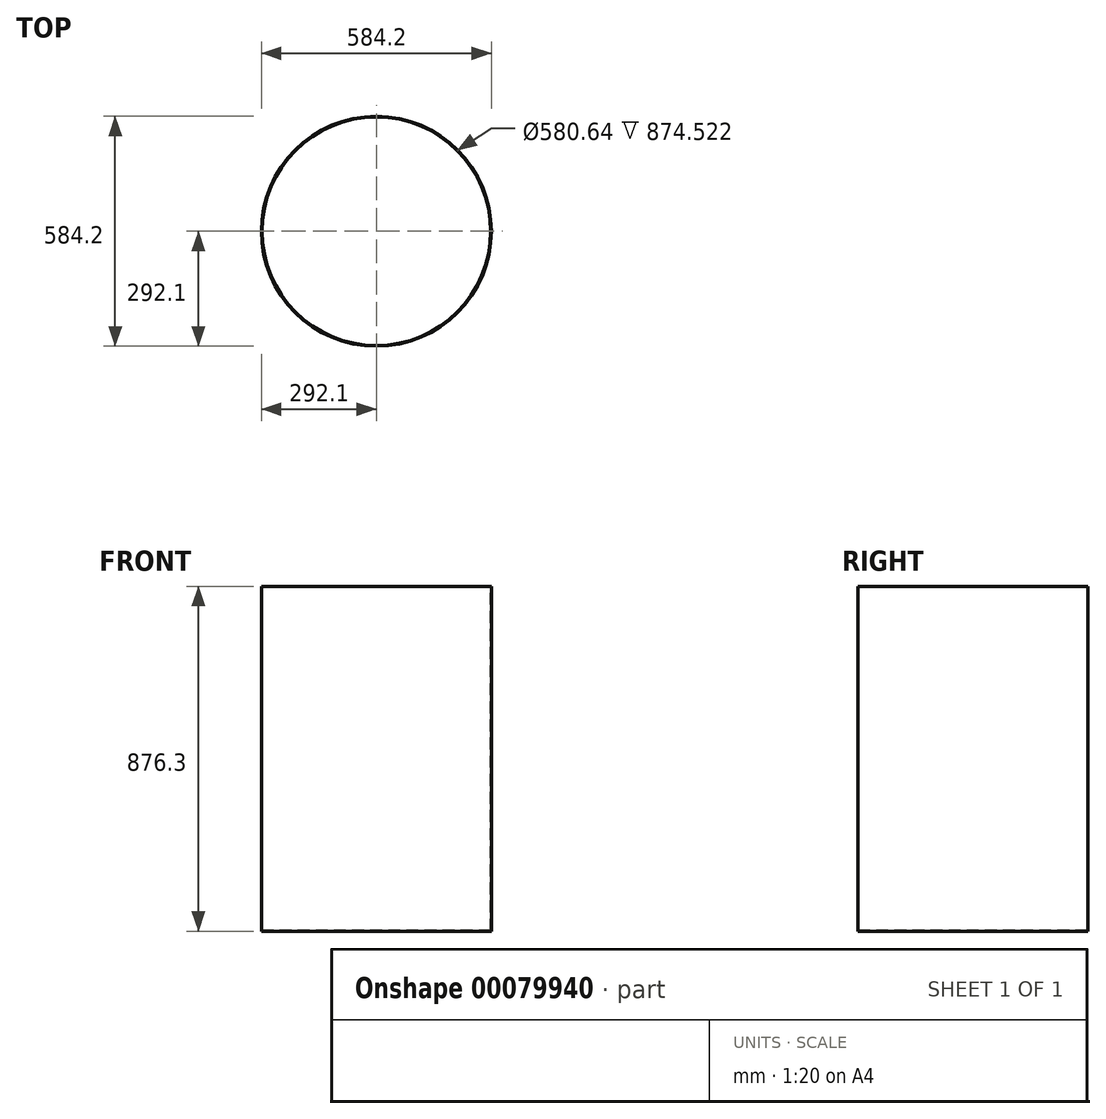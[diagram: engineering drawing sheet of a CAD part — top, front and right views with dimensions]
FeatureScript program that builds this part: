
annotation { "Feature Type Name" : "Feature", "Feature Type Description" : "" }
export const myFeature = defineFeature(function(context is Context, id is Id, definition is map)
    precondition{}
    {
        {
            var Q0;
            Q0=qCreatedBy(makeId("Right.planeOp"),FACE);
            var sketch = newSketch(context, id + "F0", { "sketchPlane" : qUnion([Q0])});
            skLineSegment(sketch, "E0", {"start": v(0, 0) * mm, "end": v(-292.1, 0) * mm});
            skLineSegment(sketch, "E1", {"start": v(-292.1, 0) * mm, "end": v(-292.1, 876.3) * mm});
            skLineSegment(sketch, "E2", {"start": v(-292.1, 876.3) * mm, "end": v(-290.32, 876.3) * mm});
            skLineSegment(sketch, "E3", {"start": v(-290.32, 876.3) * mm, "end": v(-290.32, 1.78) * mm});
            skLineSegment(sketch, "E4", {"start": v(-290.32, 1.78) * mm, "end": v(0, 1.78) * mm});
            skLineSegment(sketch, "E5", {"start": v(0, 1.78) * mm, "end": v(0, 0) * mm});
            skSolve(sketch);
        }
        {
            var Q0;
            Q0 = qSketchRegion(id + "F0", true);
            var Q1;
            Q1=sQuery(id+"F0.wireOp",EDGE,"E5");
            revolve(context, id + "F1", {"entities" : qUnion([Q0]), "axis" : qUnion([Q1]), "revolveType" : RevolveType.FULL});
        }
    });
